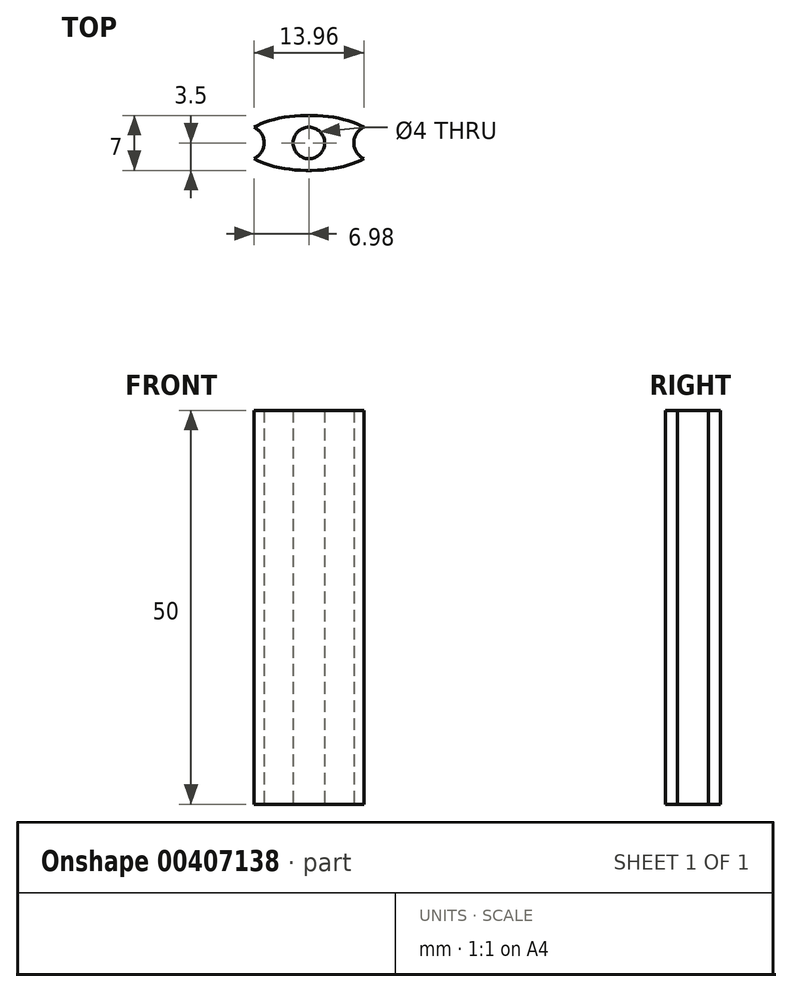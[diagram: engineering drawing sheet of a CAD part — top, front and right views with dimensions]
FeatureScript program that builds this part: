
annotation { "Feature Type Name" : "Feature", "Feature Type Description" : "" }
export const myFeature = defineFeature(function(context is Context, id is Id, definition is map)
    precondition{}
    {
        {
            var Q0;
            Q0=qCreatedBy(makeId("Top.planeOp"),FACE);
            var sketch = newSketch(context, id + "F0", { "sketchPlane" : qUnion([Q0])});
            skLineSegment(sketch, "E0", {"start": v(-10, 0) * mm, "end": v(10, 0) * mm, "construction": true});
            skLineSegment(sketch, "E1", {"start": v(0, -4) * mm, "end": v(0, 4) * mm, "construction": true});
            skEllipticalArc(sketch, "E2", {"construction": true});
            skArc(sketch, "E3", {"start": v(-6.98, -2) * mm, "mid": v(-5.7, 0) * mm, "end": v(-6.98, 2) * mm});
            skArc(sketch, "E4", {"start": v(6.98, 2) * mm, "mid": v(5.7, 0) * mm, "end": v(6.98, -2) * mm});
            skEllipticalArc(sketch, "E5", {});
            skEllipticalArc(sketch, "E6.trimOffspring", {"construction": true});
            skEllipticalArc(sketch, "E7.trimOffspring", {});
            skCircle(sketch, "E8", {"center": v(0, 0) * mm, "radius": 2 * mm});
            const initialGuessF0  = {"E2": [0, 0, -1, 0, 0.0085, 0.0035, 0.6075302167070781, 2.5340624368827154], "E5": [0, 0, -1, 0, 0.0085, 0.0035, 0.6075302167070781, 2.5340624368827154], "E6.trimOffspring": [0, 0, -1, 0, 0.0085, 0.0035, 3.749122870296872, 5.6756550904725085], "E7.trimOffspring": [0, 0, -1, 0, 0.0085, 0.0035, 3.749122870296872, 5.6756550904725085]};
            skSetInitialGuess(sketch, initialGuessF0);
            skSolve(sketch);
        }
        {
            var Q0;
            Q0=qSketchRegion(id+"F0",true);
            extrude(context, id + "F1", {"entities" : qUnion([Q0]), "depth" : 50 * mm, "offsetDistance" : 25 * mm});
        }
    });
